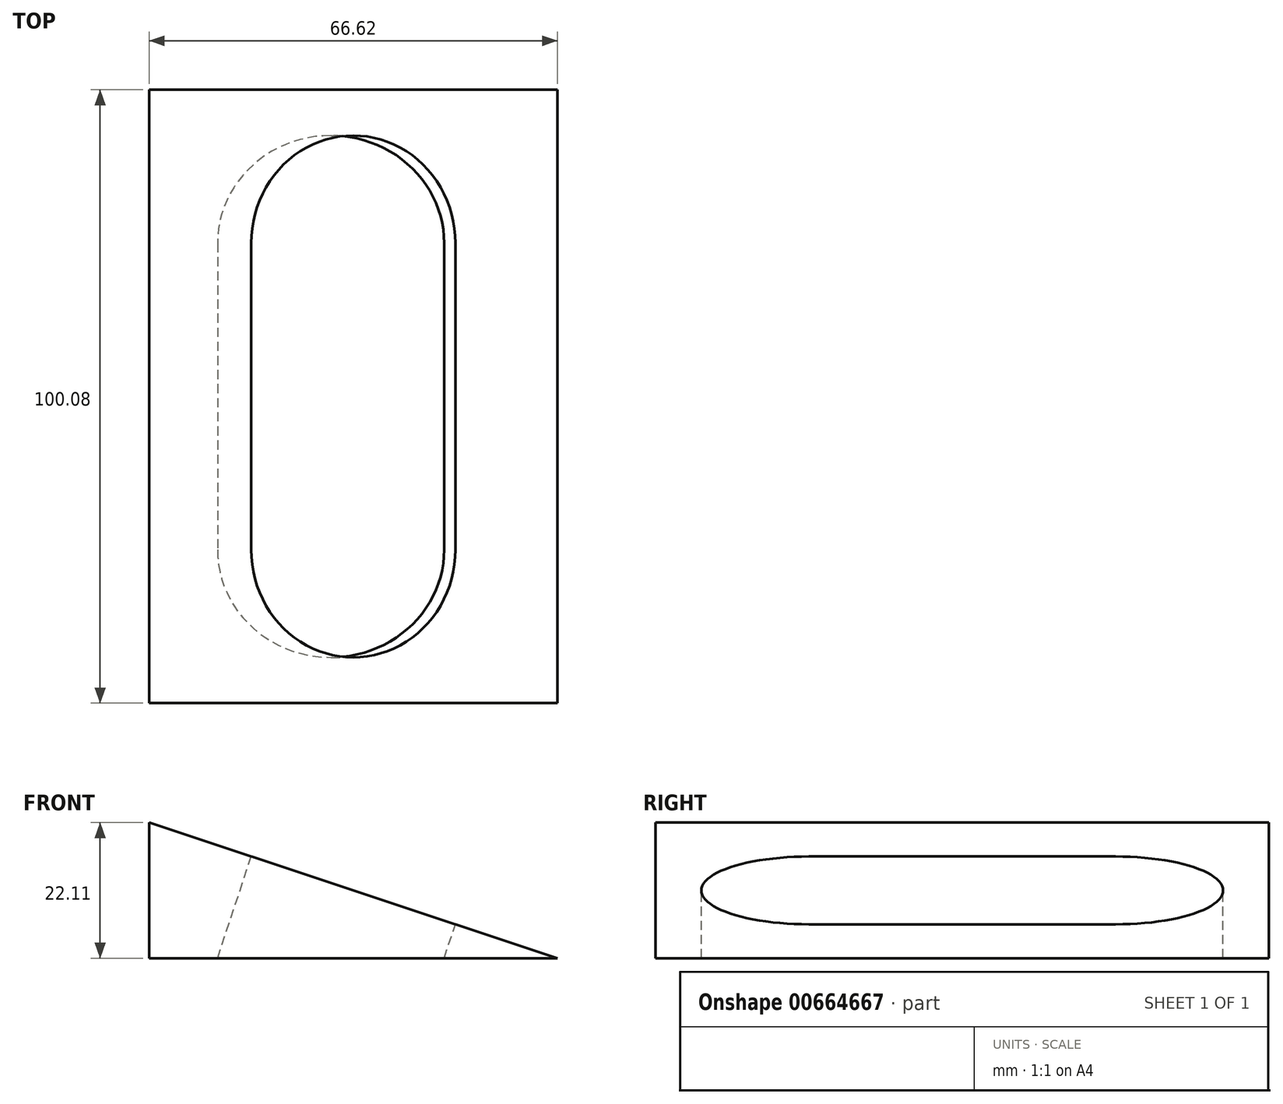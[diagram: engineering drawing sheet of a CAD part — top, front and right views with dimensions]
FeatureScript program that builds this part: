
annotation { "Feature Type Name" : "Feature", "Feature Type Description" : "" }
export const myFeature = defineFeature(function(context is Context, id is Id, definition is map)
    precondition{}
    {
        {
            var Q0;
            Q0=qCreatedBy(makeId("Front.planeOp"),FACE);
            var sketch = newSketch(context, id + "F0", { "sketchPlane" : qUnion([Q0])});
            skLineSegment(sketch, "E0", {"start": v(0, 0) * mm, "end": v(66.62, 0) * mm});
            skLineSegment(sketch, "E1", {"start": v(0, 0) * mm, "end": v(0, 22.1) * mm});
            skLineSegment(sketch, "E2", {"start": v(66.62, 0) * mm, "end": v(0, 22.1) * mm});
            skSolve(sketch);
        }
        {
            var Q0;
            Q0=makeQuery(id+"F0.imprint","IMPRINT",FACE,{"disambiguationData":[TD([[makeQuery(id+"F0.imprint","IMPRINT",EDGE,{"derivedFrom":sQuery(id+"F0.wireOp",EDGE,"E0")}),1.0]])]});
            extrude(context, id + "F1", {"entities" : qUnion([Q0]), "depth" : 100.08 * mm, "offsetDistance" : 25.4 * mm});
        }
        {
            var Q0;
            Q0=makeQuery(id+"F1.opExtrude","SWEPT_FACE",FACE,{"disambiguationData":[OSD([sQuery(id+"F0.wireOp",EDGE,"E2")])]});
            var sketch = newSketch(context, id + "F2", { "sketchPlane" : qUnion([Q0])});
            skLineSegment(sketch, "E3", {"start": v(10.59, -25.02) * mm, "end": v(10.59, -75.06) * mm});
            skLineSegment(sketch, "E4", {"start": v(28.14, -7.47) * mm, "end": v(28.14, 0) * mm});
            skLineSegment(sketch, "E5", {"start": v(45.69, -75.06) * mm, "end": v(45.69, -25.02) * mm});
            skArc(sketch, "E6", {"start": v(45.69, -25.02) * mm, "mid": v(28.14, -7.47) * mm, "end": v(10.59, -25.02) * mm});
            skArc(sketch, "E7", {"start": v(10.59, -75.06) * mm, "mid": v(28.14, -92.6) * mm, "end": v(45.69, -75.06) * mm});
            skPoint(sketch, "E8.orphan", {"position": v(-6.96, 0) * mm});
            skPoint(sketch, "E9.end.orphan", {"position": v(-6.96, -25.02) * mm});
            skPoint(sketch, "E9.start.orphan", {"position": v(-6.96, -50.04) * mm});
            skPoint(sketch, "E10.orphan", {"position": v(28.14, -50.04) * mm});
            skPoint(sketch, "E11.trimOffspring.end.orphan", {"position": v(-6.96, -75.06) * mm});
            skPoint(sketch, "E12.end.orphan", {"position": v(28.14, -100.08) * mm});
            skPoint(sketch, "E13.start.orphan", {"position": v(63.23, -75.06) * mm});
            skPoint(sketch, "E14.orphan", {"position": v(63.23, -25.02) * mm});
            skPoint(sketch, "E15.orphan", {"position": v(63.23, -50.04) * mm});
            skPoint(sketch, "E16.end.orphan", {"position": v(63.23, -100.08) * mm});
            skSolve(sketch);
        }
        {
            var Q0;
            Q0 = qSketchRegion(id + "F2", true);
            extrude(context, id + "F3", {"entities" : qUnion([Q0]), "operationType" : NewBodyOperationType.REMOVE, "oppositeDirection" : true, "depth" : 48.26 * mm, "offsetDistance" : 25.4 * mm});
        }
    });
